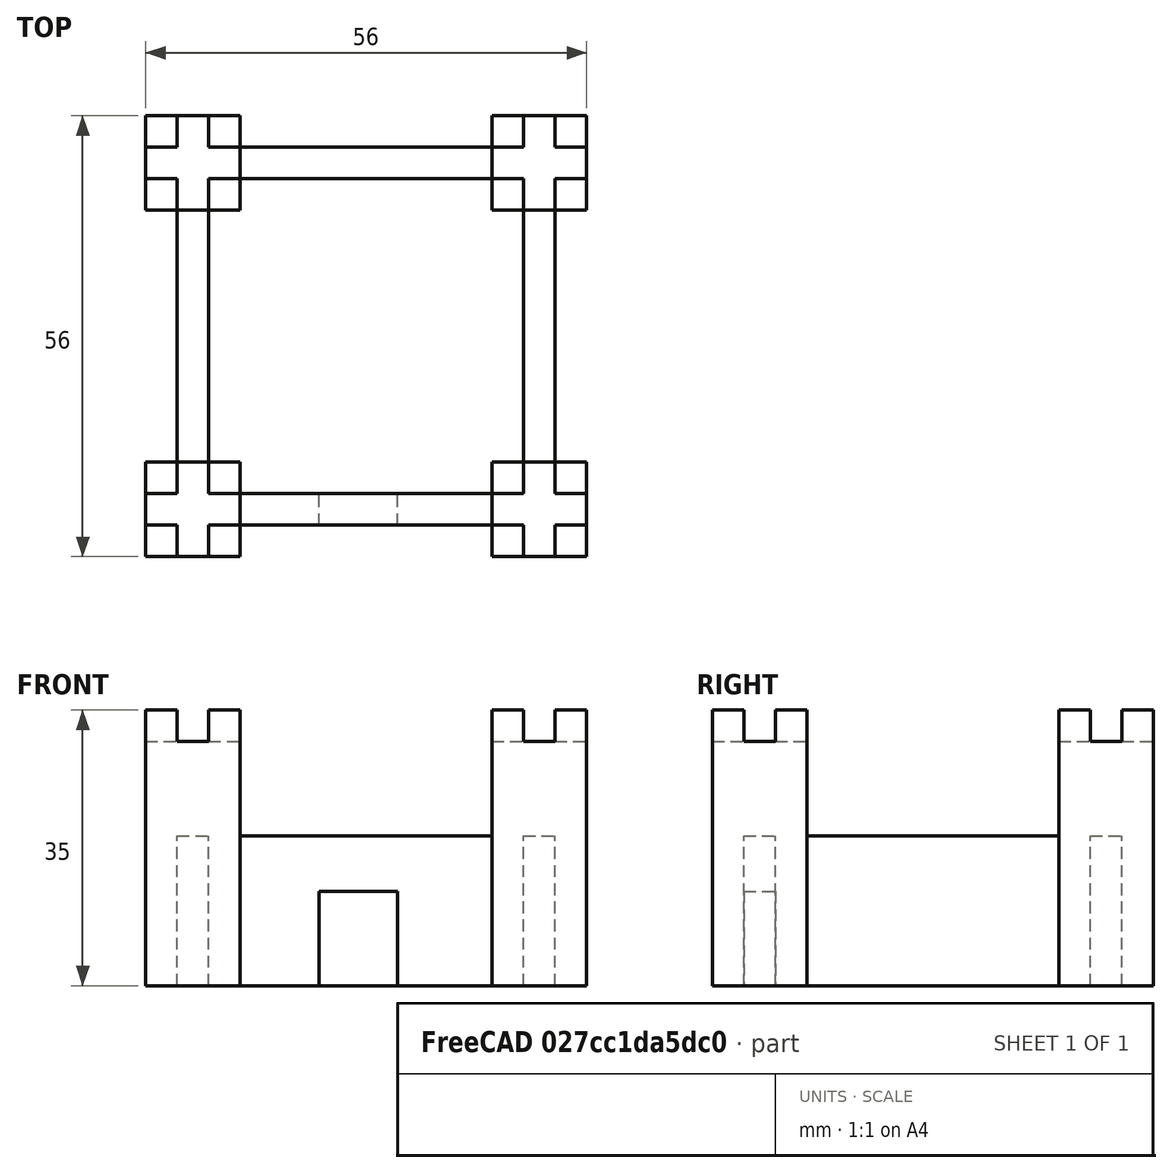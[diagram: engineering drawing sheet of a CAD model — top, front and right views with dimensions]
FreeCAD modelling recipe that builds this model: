
FCSTD DOCUMENT  (FreeCAD 1.0R38806 (Git))
Label: castle
License: All rights reserved
LicenseURL: https://en.wikipedia.org/wiki/All_rights_reserved
objects: Part::Box×17, Part::Cut×5, Part::MultiFuse×4
note: 26 computed .brp shape members not serialized (recipe doc carries the construction recipe); baked Part::Feature solids carry a one-line shape summary decoded from their .brp

FEATURE [Part::Box] Box  label="Cube"
  AttacherType = Attacher::AttachEngine3D
  Height = 35
  Length = 12
  Width = 12
FEATURE [Part::Box] Box001  label="Cube001"
  AttacherType = Attacher::AttachEngine3D
  Height = 4
  Length = 12
  Placement = pos=(0,4,31) rot=(0,0,1;0rad)
  Width = 4
FEATURE [Part::Box] Box002  label="Cube002"
  AttacherType = Attacher::AttachEngine3D
  Height = 4
  Length = 12
  Placement = pos=(8,0,31) rot=(0,0,1;1.5708rad)
  Width = 4
FEATURE [Part::MultiFuse] Fusion
  Refine = true
  Shapes = -> [Box002,Box001]
FEATURE [Part::Cut] Cut  label="tower_fl"
  Base = -> Box
  Refine = true
  Tool = -> Fusion
FEATURE [Part::Box] Box003  label="wall_l"
  AttacherType = Attacher::AttachEngine3D
  Height = 19
  Length = 4
  Placement = pos=(4,12,0) rot=(0,0,1;0rad)
  Width = 32
FEATURE [Part::Box] Box004  label="Cube003"
  AttacherType = Attacher::AttachEngine3D
  Height = 35
  Length = 12
  Width = 12
FEATURE [Part::Box] Box005  label="Cube004"
  AttacherType = Attacher::AttachEngine3D
  Height = 4
  Length = 12
  Placement = pos=(0,4,31) rot=(0,0,1;0rad)
  Width = 4
FEATURE [Part::Box] Box006  label="Cube005"
  AttacherType = Attacher::AttachEngine3D
  Height = 4
  Length = 12
  Placement = pos=(8,0,31) rot=(0,0,1;1.5708rad)
  Width = 4
FEATURE [Part::MultiFuse] Fusion001
  Refine = true
  Shapes = -> [Box006,Box005]
FEATURE [Part::Cut] Cut001  label="tower_bl"
  Base = -> Box004
  Placement = pos=(0,44,0) rot=(0,0,1;0rad)
  Refine = true
  Tool = -> Fusion001
FEATURE [Part::Box] Box007  label="wall_b"
  AttacherType = Attacher::AttachEngine3D
  Height = 19
  Length = 4
  Placement = pos=(44,48,0) rot=(0,0,1;1.5708rad)
  Width = 32
FEATURE [Part::Box] Box008  label="Cube006"
  AttacherType = Attacher::AttachEngine3D
  Height = 35
  Length = 12
  Width = 12
FEATURE [Part::Box] Box009  label="Cube007"
  AttacherType = Attacher::AttachEngine3D
  Height = 4
  Length = 12
  Placement = pos=(0,4,31) rot=(0,0,1;0rad)
  Width = 4
FEATURE [Part::Box] Box010  label="Cube008"
  AttacherType = Attacher::AttachEngine3D
  Height = 4
  Length = 12
  Placement = pos=(8,0,31) rot=(0,0,1;1.5708rad)
  Width = 4
FEATURE [Part::MultiFuse] Fusion002
  Refine = true
  Shapes = -> [Box010,Box009]
FEATURE [Part::Cut] Cut002  label="tower_br"
  Base = -> Box008
  Placement = pos=(44,44,0) rot=(0,0,1;0rad)
  Refine = true
  Tool = -> Fusion002
FEATURE [Part::Box] Box011  label="wall_r"
  AttacherType = Attacher::AttachEngine3D
  Height = 19
  Length = 4
  Placement = pos=(48,12,0) rot=(0,0,1;0rad)
  Width = 32
FEATURE [Part::Box] Box012  label="Cube009"
  AttacherType = Attacher::AttachEngine3D
  Height = 35
  Length = 12
  Width = 12
FEATURE [Part::Box] Box013  label="Cube010"
  AttacherType = Attacher::AttachEngine3D
  Height = 4
  Length = 12
  Placement = pos=(0,4,31) rot=(0,0,1;0rad)
  Width = 4
FEATURE [Part::Box] Box014  label="Cube011"
  AttacherType = Attacher::AttachEngine3D
  Height = 4
  Length = 12
  Placement = pos=(8,0,31) rot=(0,0,1;1.5708rad)
  Width = 4
FEATURE [Part::MultiFuse] Fusion003
  Refine = true
  Shapes = -> [Box014,Box013]
FEATURE [Part::Cut] Cut003  label="tower_fr"
  Base = -> Box012
  Placement = pos=(44,0,0) rot=(0,0,1;0rad)
  Refine = true
  Tool = -> Fusion003
FEATURE [Part::Box] Box015  label="wall_f"
  AttacherType = Attacher::AttachEngine3D
  Height = 19
  Length = 4
  Placement = pos=(44,4,0) rot=(0,0,1;1.5708rad)
  Width = 32
FEATURE [Part::Box] Box016  label="Cube012"
  AttacherType = Attacher::AttachEngine3D
  Height = 12
  Length = 10
  Placement = pos=(22,0,0) rot=(0,0,1;0rad)
  Width = 10
FEATURE [Part::Cut] Cut004
  Base = -> Box015
  Refine = true
  Tool = -> Box016
